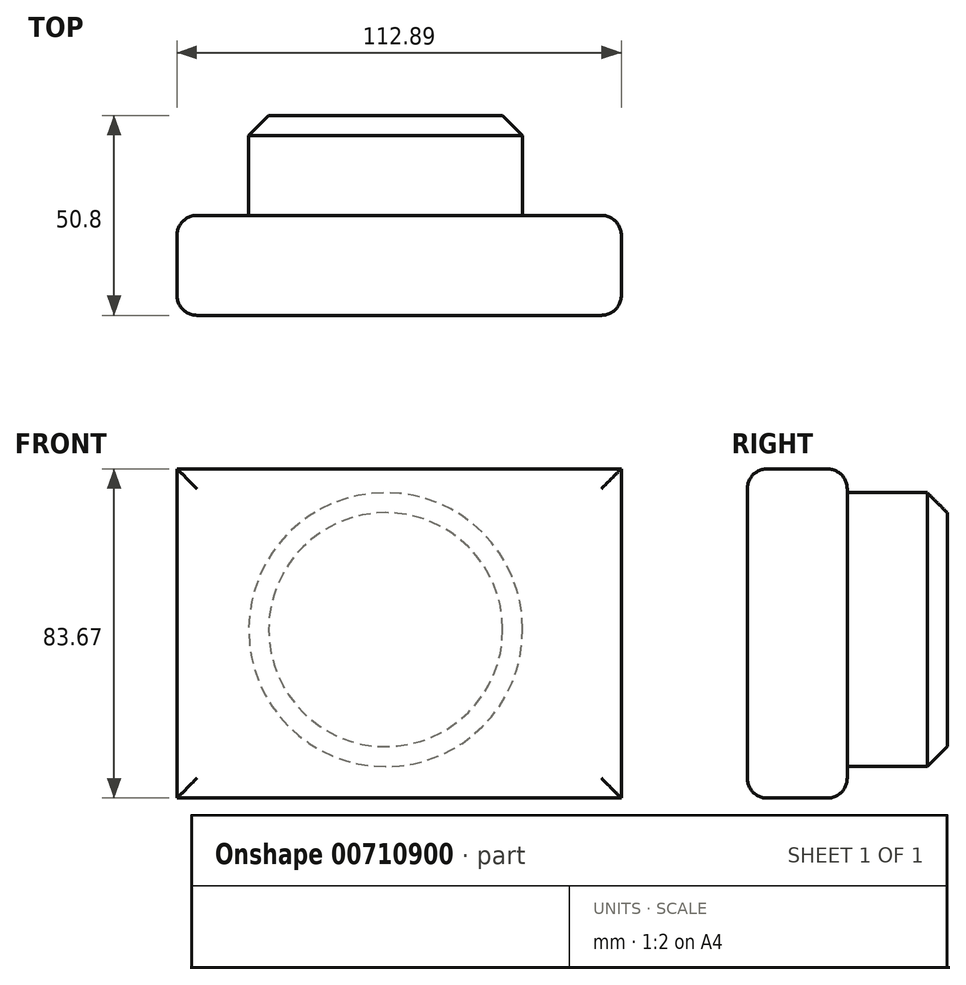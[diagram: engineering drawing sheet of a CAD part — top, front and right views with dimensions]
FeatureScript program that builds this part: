
annotation { "Feature Type Name" : "Feature", "Feature Type Description" : "" }
export const myFeature = defineFeature(function(context is Context, id is Id, definition is map)
    precondition{}
    {
        {
            var Q0;
            Q0=qCreatedBy(makeId("Front.planeOp"),FACE);
            var sketch = newSketch(context, id + "F0", { "sketchPlane" : qUnion([Q0])});
            skLineSegment(sketch, "E0", {"start": v(0, 0) * mm, "end": v(0, 0) * mm});
            skLineSegment(sketch, "E1", {"start": v(0, 0) * mm, "end": v(94.37, 0) * mm});
            skLineSegment(sketch, "E2", {"start": v(94.37, 0) * mm, "end": v(2.82, -0.6) * mm});
            skLineSegment(sketch, "E3", {"start": v(2.82, -0.6) * mm, "end": v(3.39, -0.43) * mm});
            skLineSegment(sketch, "E4", {"start": v(112.89, 83.67) * mm, "end": v(112.89, 0) * mm});
            skLineSegment(sketch, "E5", {"start": v(112.89, 0) * mm, "end": v(94.37, 0) * mm});
            skLineSegment(sketch, "E6", {"start": v(112.89, 83.67) * mm, "end": v(0, 83.67) * mm});
            skLineSegment(sketch, "E7", {"start": v(0, 83.67) * mm, "end": v(0, 0) * mm});
            skSolve(sketch);
        }
        {
            var Q0;
            Q0=makeQuery(id+"F0.imprint","IMPRINT",FACE,{"disambiguationData":[TD([[makeQuery(id+"F0.imprint","IMPRINT",EDGE,{"derivedFrom":sQuery(id+"F0.wireOp",EDGE,"E1")}),1.0]])]});
            extrude(context, id + "F1", {"entities" : qUnion([Q0]), "depth" : 25.4 * mm, "offsetDistance" : 25.4 * mm});
        }
        {
            var Q0;
            Q0=makeQuery(id+"F1.opExtrude","CAP_EDGE",EDGE,{"disambiguationData":[OSD([sQuery(id+"F0.wireOp",EDGE,"E4")])],"isStart":true});
            var Q1;
            Q1=makeQuery(id+"F1.opExtrude","CAP_FACE",FACE,{"disambiguationData":[OSD([sQuery(id+"F0.wireOp",EDGE,"E1"),sQuery(id+"F0.wireOp",EDGE,"E4"),sQuery(id+"F0.wireOp",EDGE,"E5"),sQuery(id+"F0.wireOp",EDGE,"E6"),sQuery(id+"F0.wireOp",EDGE,"E7")])],"isStart":true});
            fillet(context, id + "F2", {"entities" : qUnion([Q0, Q1]), "radius" : 5.08 * mm, "tangentPropagation" : true, "allowEdgeOverflow" : false});
        }
        {
            var Q0;
            Q0=makeQuery(id+"F1.opExtrude","CAP_EDGE",EDGE,{"disambiguationData":[OSD([sQuery(id+"F0.wireOp",EDGE,"E4")])],"isStart":false});
            var Q1;
            Q1=makeQuery(id+"F1.opExtrude","CAP_EDGE",EDGE,{"disambiguationData":[OSD([sQuery(id+"F0.wireOp",EDGE,"E6")])],"isStart":false});
            var Q2;
            Q2=makeQuery(id+"F1.opExtrude","CAP_EDGE",EDGE,{"disambiguationData":[OSD([sQuery(id+"F0.wireOp",EDGE,"E7")])],"isStart":false});
            var Q3;
            Q3=makeQuery(id+"F1.opExtrude","CAP_EDGE",EDGE,{"disambiguationData":[OSD([sQuery(id+"F0.wireOp",EDGE,"E1"),sQuery(id+"F0.wireOp",EDGE,"E5")])],"isStart":false});
            fillet(context, id + "F3", {"entities" : qUnion([Q0, Q1, Q2, Q3]), "radius" : 5.08 * mm, "tangentPropagation" : true, "allowEdgeOverflow" : false});
        }
        {
            var Q0;
            Q0=makeQuery(id+"F1.opExtrude","CAP_FACE",FACE,{"disambiguationData":[OSD([sQuery(id+"F0.wireOp",EDGE,"E1"),sQuery(id+"F0.wireOp",EDGE,"E4"),sQuery(id+"F0.wireOp",EDGE,"E5"),sQuery(id+"F0.wireOp",EDGE,"E6"),sQuery(id+"F0.wireOp",EDGE,"E7")])],"isStart":true});
            var sketch = newSketch(context, id + "F4", { "sketchPlane" : qUnion([Q0])});
            skSolve(sketch);
        }
        {
            var Q0;
            {var subQ0=sQuery(id+"F0.wireOp",EDGE,"E7");var subQ1=sQuery(id+"F0.wireOp",EDGE,"E6");var subQ2=sQuery(id+"F0.wireOp",EDGE,"E5");var subQ3=sQuery(id+"F0.wireOp",EDGE,"E4");var subQ4=sQuery(id+"F0.wireOp",EDGE,"E1");var subQ5=makeQuery(id+"F1.opExtrude","CAP_FACE",FACE,{"disambiguationData":[OSD([subQ4,subQ3,subQ2,subQ1,subQ0])],"isStart":true});Q0=makeQuery(id+"F4.imprint","IMPRINT",FACE,{"disambiguationData":[TD([[makeQuery(id+"F4.imprint","IMPRINT",EDGE,{"derivedFrom":makeQuery(id+"F2.opFillet","BLEND_EDGE",EDGE,{"blendedFrom":[makeQuery(id+"F1.opExtrude","CAP_EDGE",EDGE,{"disambiguationData":[OSD([subQ3])],"isStart":true}),subQ5],"blendedInto":[subQ5]})}),1.0]])]});}
            var sketch = newSketch(context, id + "F5", { "sketchPlane" : qUnion([Q0])});
            skCircle(sketch, "E8", {"center": v(-53.03, 42.8) * mm, "radius": 34.8 * mm});
            skSolve(sketch);
        }
        {
            var Q0;
            Q0=makeQuery(id+"F5.imprint","IMPRINT",FACE,{"disambiguationData":[TD([[makeQuery(id+"F5.imprint","IMPRINT",EDGE,{"derivedFrom":sQuery(id+"F5.wireOp",EDGE,"E8")}),1.0]])]});
            extrude(context, id + "F6", {"entities" : qUnion([Q0]), "operationType" : NewBodyOperationType.ADD, "depth" : 25.4 * mm, "offsetDistance" : 25.4 * mm});
        }
        {
            var Q0;
            Q0=makeQuery(id+"F6.opExtrude","CAP_EDGE",EDGE,{"disambiguationData":[OSD([sQuery(id+"F5.wireOp",EDGE,"E8")])],"isStart":false});
            chamfer(context, id + "F7", {"entities" : qUnion([Q0]), "width" : 5.08 * mm, "tangentPropagation" : true});
        }
    });
